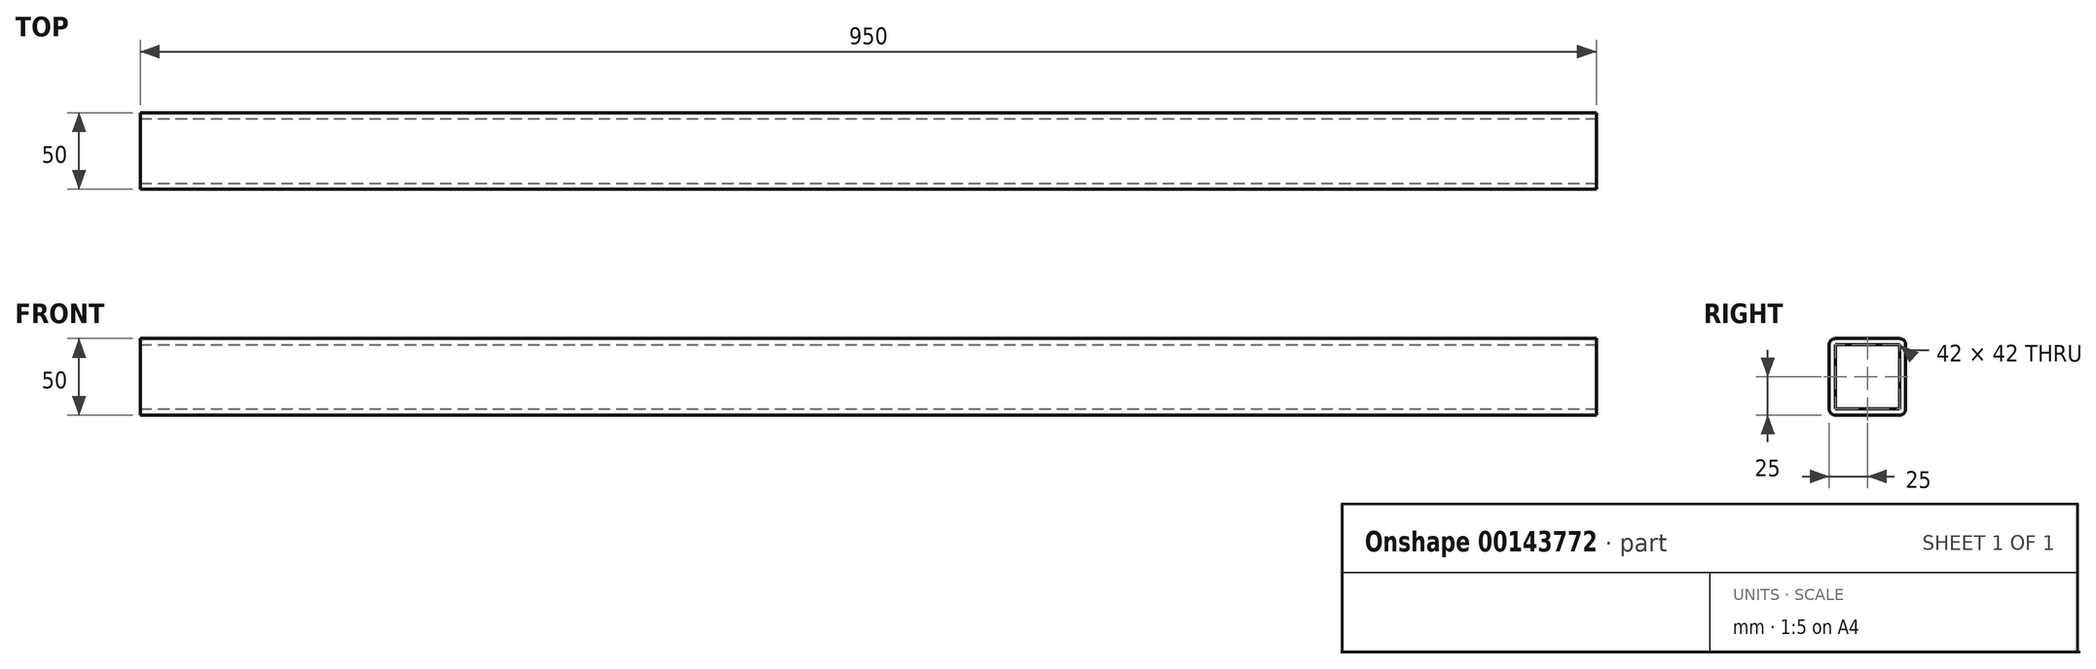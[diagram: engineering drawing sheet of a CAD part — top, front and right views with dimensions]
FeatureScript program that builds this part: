
annotation { "Feature Type Name" : "Feature", "Feature Type Description" : "" }
export const myFeature = defineFeature(function(context is Context, id is Id, definition is map)
    precondition{}
    {
        {
            var Q0;
            Q0=qCreatedBy(makeId("Right.planeOp"),FACE);
            var sketch = newSketch(context, id + "F0", { "sketchPlane" : qUnion([Q0])});
            skLineSegment(sketch, "E0.bottom", {"start": v(-21, 25) * mm, "end": v(21, 25) * mm});
            skLineSegment(sketch, "E0.top", {"start": v(-21, -25) * mm, "end": v(21, -25) * mm});
            skLineSegment(sketch, "E0.left", {"start": v(-25, 21) * mm, "end": v(-25, -21) * mm});
            skLineSegment(sketch, "E0.right", {"start": v(25, 21) * mm, "end": v(25, -21) * mm});
            skPoint(sketch, "E1.visualSharp", {"position": v(-25, 25) * mm});
            skArc(sketch, "E1.filletArc", {"start": v(-21, 25) * mm, "mid": v(-23.83, 23.83) * mm, "end": v(-25, 21) * mm});
            skPoint(sketch, "E2.visualSharp", {"position": v(-25, -25) * mm});
            skArc(sketch, "E2.filletArc", {"start": v(-25, -21) * mm, "mid": v(-23.83, -23.83) * mm, "end": v(-21, -25) * mm});
            skPoint(sketch, "E3.visualSharp", {"position": v(25, -25) * mm});
            skArc(sketch, "E3.filletArc", {"start": v(21, -25) * mm, "mid": v(23.83, -23.83) * mm, "end": v(25, -21) * mm});
            skPoint(sketch, "E4.visualSharp", {"position": v(25, 25) * mm});
            skArc(sketch, "E4.filletArc", {"start": v(25, 21) * mm, "mid": v(23.83, 23.83) * mm, "end": v(21, 25) * mm});
            skLineSegment(sketch, "E5.0", {"start": v(21, 21) * mm, "end": v(21, -21) * mm});
            skLineSegment(sketch, "E5.1", {"start": v(-21, 21) * mm, "end": v(21, 21) * mm});
            skLineSegment(sketch, "E5.2", {"start": v(-21, 21) * mm, "end": v(-21, -21) * mm});
            skLineSegment(sketch, "E5.3", {"start": v(-21, -21) * mm, "end": v(21, -21) * mm});
            skSolve(sketch);
        }
        {
            var Q0;
            Q0=makeQuery(id+"F0.imprint","IMPRINT",FACE,{"disambiguationData":[TD([[makeQuery(id+"F0.imprint","IMPRINT",EDGE,{"derivedFrom":sQuery(id+"F0.wireOp",EDGE,"E0.bottom")}),-1.0]])]});
            extrude(context, id + "F1", {"entities" : qUnion([Q0]), "endBound" : BoundingType.SYMMETRIC, "oppositeDirection" : true, "depth" : 950 * mm});
        }
    });
